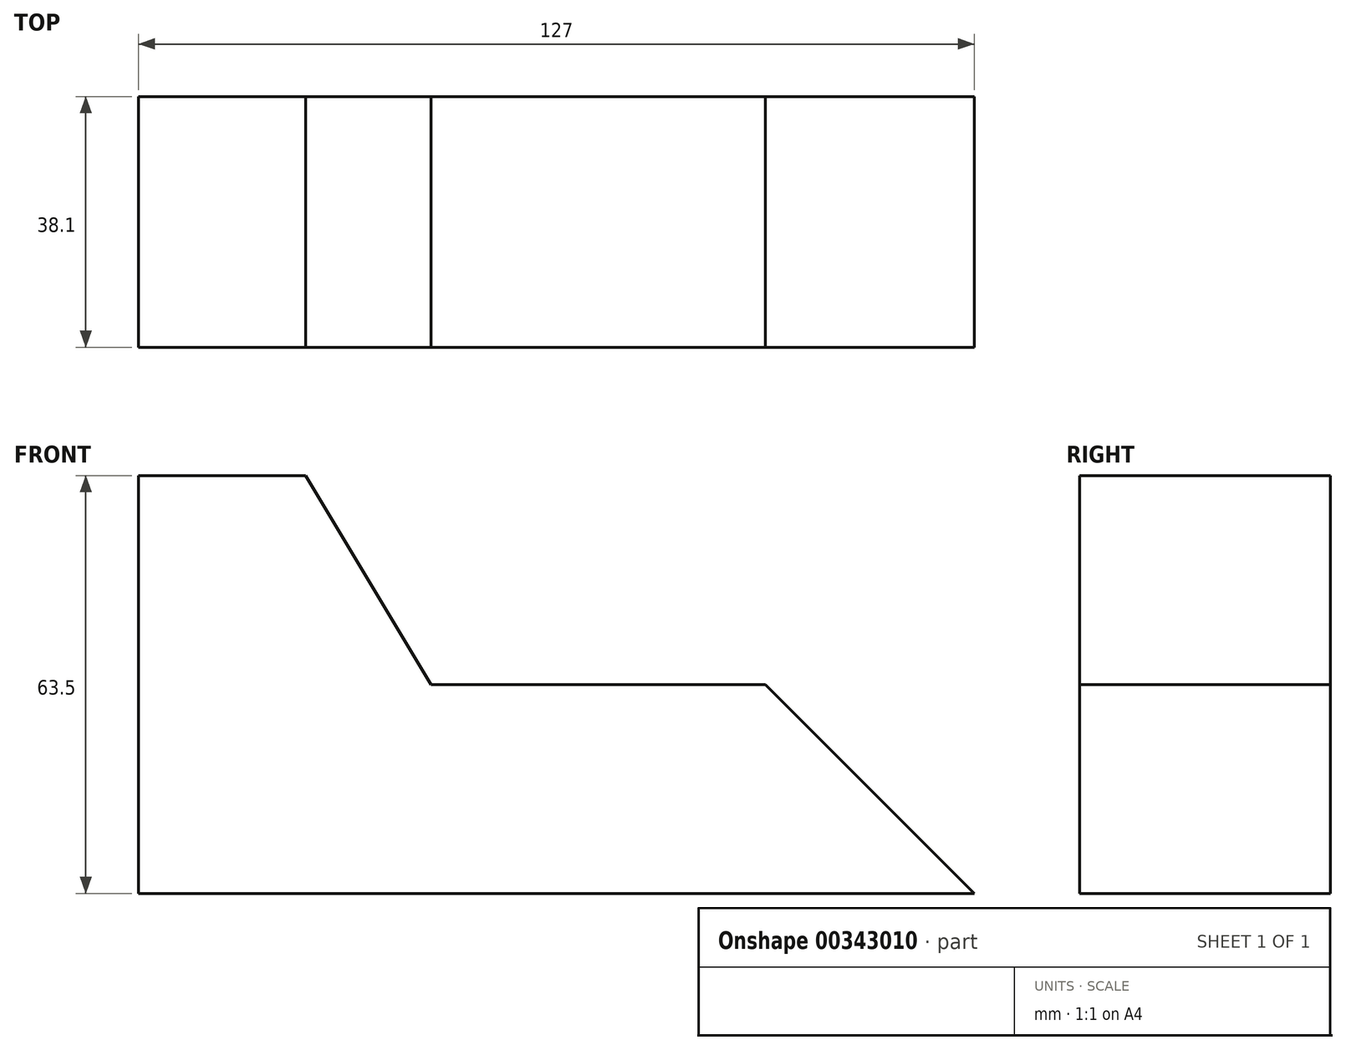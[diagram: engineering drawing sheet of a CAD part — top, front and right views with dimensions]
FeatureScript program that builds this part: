
annotation { "Feature Type Name" : "Feature", "Feature Type Description" : "" }
export const myFeature = defineFeature(function(context is Context, id is Id, definition is map)
    precondition{}
    {
        {
            var Q0;
            Q0=qCreatedBy(makeId("Front.planeOp"),FACE);
            var sketch = newSketch(context, id + "F0", { "sketchPlane" : qUnion([Q0])});
            skLineSegment(sketch, "E0", {"start": v(56.85, -31.75) * mm, "end": v(-70.15, -31.75) * mm});
            skLineSegment(sketch, "E1", {"start": v(-70.15, -31.75) * mm, "end": v(-70.15, 31.75) * mm});
            skLineSegment(sketch, "E2", {"start": v(-70.15, 31.75) * mm, "end": v(-44.75, 31.75) * mm});
            skLineSegment(sketch, "E3", {"start": v(56.85, -31.75) * mm, "end": v(25.1, 0) * mm});
            skLineSegment(sketch, "E4", {"start": v(-44.75, 31.75) * mm, "end": v(-25.7, 0) * mm});
            skLineSegment(sketch, "E5", {"start": v(-25.7, 0) * mm, "end": v(25.1, 0) * mm});
            skSolve(sketch);
        }
        {
            var Q0;
            Q0=makeQuery(id+"F0.imprint","IMPRINT",FACE,{"disambiguationData":[TD([[makeQuery(id+"F0.imprint","IMPRINT",EDGE,{"derivedFrom":sQuery(id+"F0.wireOp",EDGE,"E0")}),-1.0]])]});
            extrude(context, id + "F1", {"entities" : qUnion([Q0]), "depth" : 38.1 * mm});
        }
    });
